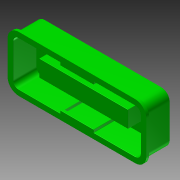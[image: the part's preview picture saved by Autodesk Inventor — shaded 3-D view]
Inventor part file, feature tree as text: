
AUTODESK INVENTOR PART (.ipt)
format: ipt  version: 2015 (Build 190159000, 159)  size: 241,152 bytes
history: native  units: in
note: dims shown in document units (in); Inventor stores cm internally (conversion verified against a paired STEP export)
features: fillet x7, extrude x5, sketch x5, mirror x4, plane x3, shell x2
ambient origin geometry x8: Origin, YZ Plane, XZ Plane, XY Plane, X Axis, Y Axis, Z Axis, Center Point
bodies: Solid1 (feature_tree)
feature tree (26):
  extrude  "Extrusion1"  Depth=0.5in
  fillet  "Fillet1"  Radius=0.47in
  shell  "Shell1"  Thickness=0.2in
  sketch  "Sketch2"  dims[d7=0.46in d8=0.2283in]
  plane  "Work Plane1"
  shell  "Shell2"  Thickness=0.1in
  extrude  "Extrusion5"  Depth=0.2283in
  plane  "Work Plane3"
  extrude  "Extrusion6"  Depth=0.47in TaperAngle=0.0deg
  plane  "Work Plane4"
  extrude  "Extrusion7"  Depth=0.01in
  fillet  "Fillet8"  Radius=0.05in
  mirror  "Mirror3"
  mirror  "Mirror4"
  fillet  "Fillet6"  Radius=0.05in
  fillet  "Fillet3"  Radius=0.445in
  fillet  "Fillet4"  Radius=0.05in
  extrude  "Extrusion2"  Depth=0.05in TaperAngle=0.0deg
  fillet  "Fillet2"  [1 undecoded]
  fillet  "Fillet7"  Radius=0.05in
  mirror  "Mirror1"
  mirror  "Mirror2"
  sketch  "Sketch1"  dims[d0=1.25in d1=0.5in d2=0.47in d3=0.0in d4=0.2in d5=0.1in]
  sketch  "Sketch4"  dims[d9=-0.033in d10=0.47in d11=0.0in]
  sketch  "Sketch5"  dims[d12=0.005in d13=0.01in d18=0.05in d23=0.05in d26=0.445in d28=0.05in]
  sketch  "Sketch6"  dims[d29=0.3in d30=0.05in d31=0.0in d32=-0.05in d33=0.05in d34=0.03in d35=0.4325in d36=0.0in d37=0.3in d38=0.8in d39=0.15in d40=0.005in d41=0.0in d42=0.005in]
note: 1 required parameter value undecoded (feature->parameter linkage not recoverable at this tier; creation-order binding heuristic only, values carry confidence <= 0.55)
